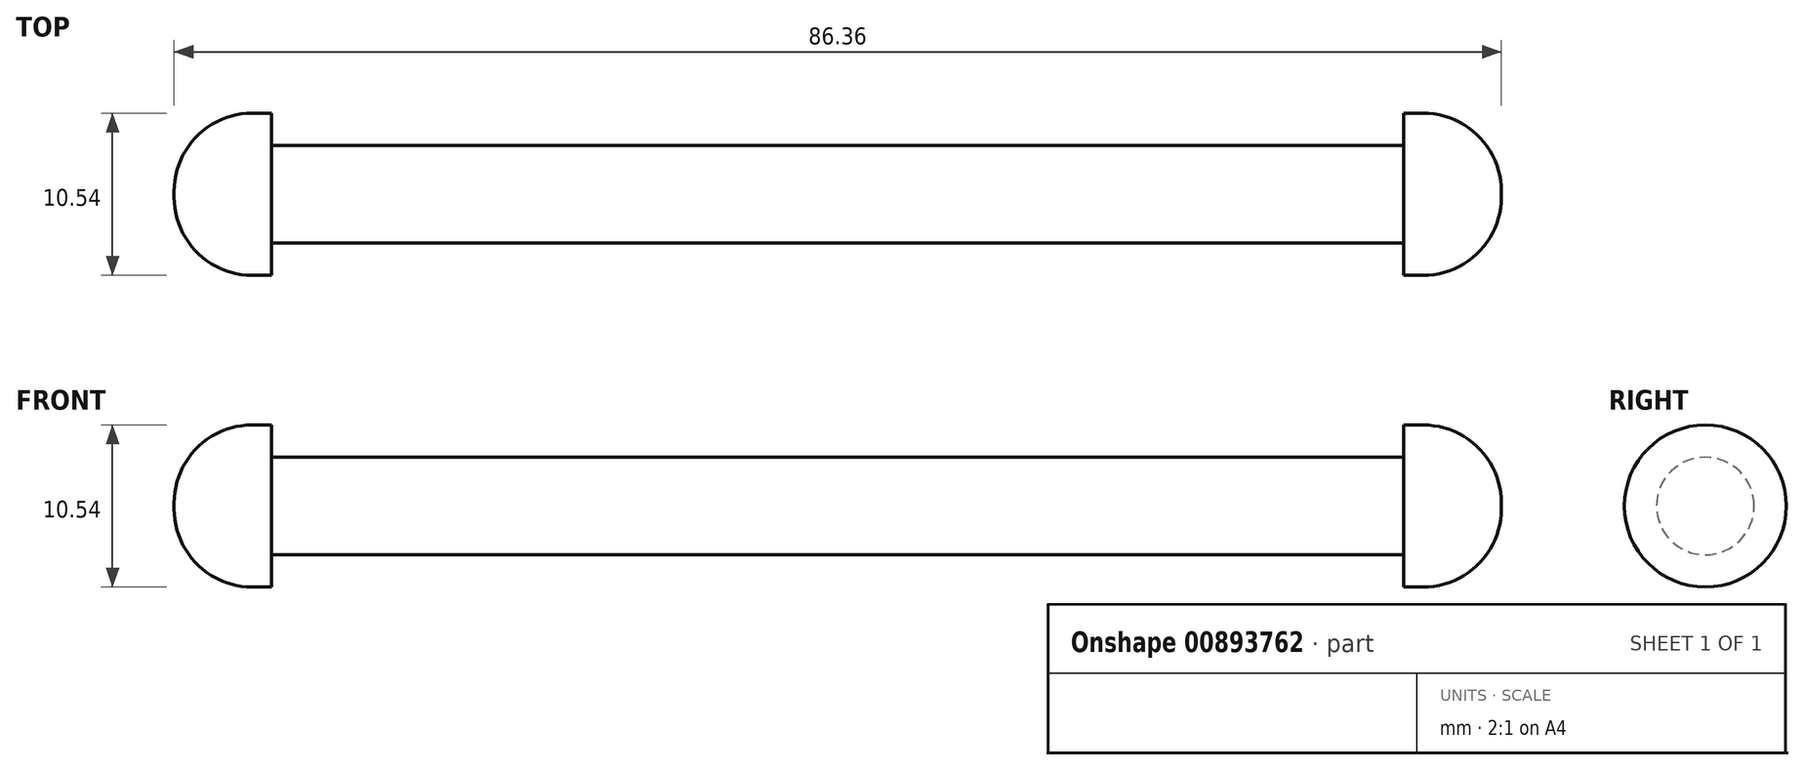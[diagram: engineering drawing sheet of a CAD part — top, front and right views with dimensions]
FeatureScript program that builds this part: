
annotation { "Feature Type Name" : "Feature", "Feature Type Description" : "" }
export const myFeature = defineFeature(function(context is Context, id is Id, definition is map)
    precondition{}
    {
        {
            var Q0;
            Q0=qCreatedBy(makeId("Right.planeOp"),FACE);
            var sketch = newSketch(context, id + "F0", { "sketchPlane" : qUnion([Q0])});
            skCircle(sketch, "E0", {"center": v(0, 0) * mm, "radius": 3.18 * mm});
            skSolve(sketch);
        }
        {
            var Q0;
            Q0=qSketchRegion(id+"F0",true);
            extrude(context, id + "F1", {"entities" : qUnion([Q0]), "depth" : 36.83 * mm, "offsetDistance" : 25.4 * mm, "hasSecondDirection" : true, "secondDirectionOppositeDirection" : true, "secondDirectionDepth" : 36.83 * mm});
        }
        {
            var Q0;
            Q0=makeQuery(id+"F1.opExtrude","CAP_FACE",FACE,{"disambiguationData":[OSD([sQuery(id+"F0.wireOp",EDGE,"E0")])],"isStart":false});
            var sketch = newSketch(context, id + "F2", { "sketchPlane" : qUnion([Q0])});
            skCircle(sketch, "E1", {"center": v(0, 0) * mm, "radius": 5.27 * mm});
            skSolve(sketch);
        }
        {
            var Q0;
            Q0=qSketchRegion(id+"F2",true);
            extrude(context, id + "F3", {"entities" : qUnion([Q0]), "operationType" : NewBodyOperationType.ADD, "depth" : 6.35 * mm, "offsetDistance" : 25.4 * mm});
        }
        {
            var Q0;
            Q0=makeQuery(id+"F1.opExtrude","CAP_FACE",FACE,{"disambiguationData":[OSD([sQuery(id+"F0.wireOp",EDGE,"E0")])],"isStart":true});
            var sketch = newSketch(context, id + "F4", { "sketchPlane" : qUnion([Q0])});
            skCircle(sketch, "E2", {"center": v(0, 0) * mm, "radius": 5.27 * mm});
            skSolve(sketch);
        }
        {
            var Q0;
            Q0=qSketchRegion(id+"F4",true);
            extrude(context, id + "F5", {"entities" : qUnion([Q0]), "operationType" : NewBodyOperationType.ADD, "depth" : 6.35 * mm, "offsetDistance" : 25.4 * mm});
        }
        {
            var Q0;
            Q0=makeQuery(id+"F3.opExtrude","CAP_FACE",FACE,{"disambiguationData":[OSD([sQuery(id+"F2.wireOp",EDGE,"E1")])],"isStart":false});
            var Q1;
            Q1=makeQuery(id+"F5.opExtrude","CAP_FACE",FACE,{"disambiguationData":[OSD([sQuery(id+"F4.wireOp",EDGE,"E2")])],"isStart":false});
            fillet(context, id + "F6", {"entities" : qUnion([Q0, Q1]), "radius" : 5.08 * mm, "tangentPropagation" : true, "allowEdgeOverflow" : false});
        }
    });
